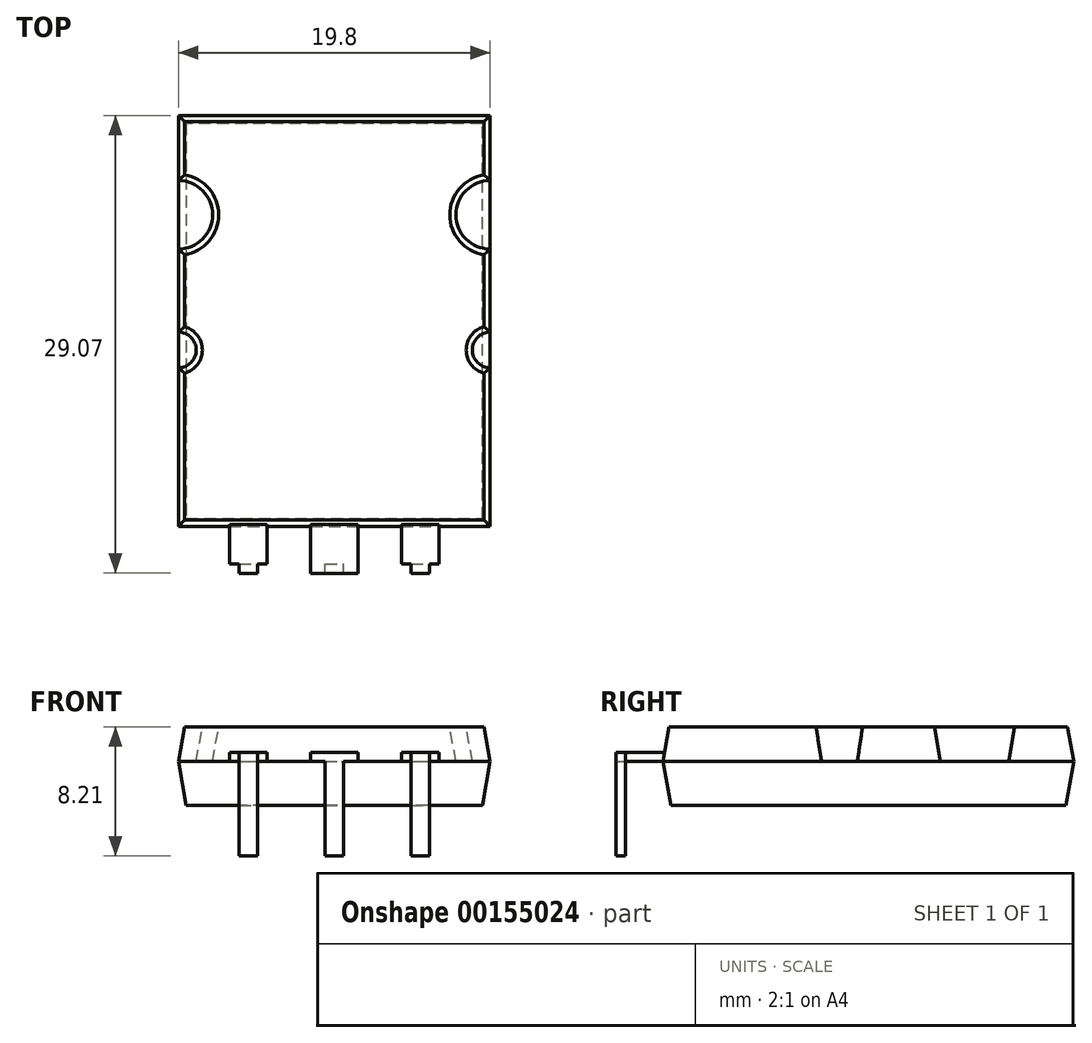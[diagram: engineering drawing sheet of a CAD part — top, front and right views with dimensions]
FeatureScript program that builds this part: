
annotation { "Feature Type Name" : "Feature", "Feature Type Description" : "" }
export const myFeature = defineFeature(function(context is Context, id is Id, definition is map)
    precondition{}
    {
        {
            assignVariable(context, id + "F0", {"name" : "A", "anyValue" : 5});
        }
        {
            assignVariable(context, id + "F1", {"name" : "A1", "anyValue" : 2.8});
        }
        {
            assignVariable(context, id + "F2", {"name" : "c", "anyValue" : .585});
        }
        {
            var Q0;
            Q0=qCreatedBy(makeId("Top.planeOp"),FACE);
            var sketch = newSketch(context, id + "F3", { "sketchPlane" : qUnion([Q0])});
            skLineSegment(sketch, "E0.right", {"start": v(9.9, 26.09) * mm, "end": v(9.9, 21.96) * mm});
            skArc(sketch, "E1", {"start": v(9.9, 21.96) * mm, "mid": v(7.73, 19.79) * mm, "end": v(9.9, 17.61) * mm});
            skArc(sketch, "E2", {"start": v(9.9, 12.33) * mm, "mid": v(8.77, 11.2) * mm, "end": v(9.9, 10.07) * mm});
            skLineSegment(sketch, "E3.trimOffspring", {"start": v(9.9, 17.61) * mm, "end": v(9.9, 12.33) * mm});
            skLineSegment(sketch, "E4.trimOffspring", {"start": v(9.9, 10.07) * mm, "end": v(9.9, 0) * mm});
            skArc(sketch, "E5.MirrorCS", {"start": v(-9.9, 12.33) * mm, "mid": v(-8.77, 11.2) * mm, "end": v(-9.9, 10.07) * mm});
            skLineSegment(sketch, "E6.MirrorCS", {"start": v(-9.9, 17.61) * mm, "end": v(-9.9, 12.33) * mm});
            skArc(sketch, "E7.MirrorCS", {"start": v(-9.9, 21.96) * mm, "mid": v(-7.73, 19.79) * mm, "end": v(-9.9, 17.61) * mm});
            skLineSegment(sketch, "E8.MirrorCS", {"start": v(-9.9, 26.09) * mm, "end": v(-9.9, 21.96) * mm});
            skLineSegment(sketch, "E9.MirrorCS", {"start": v(-9.9, 10.07) * mm, "end": v(-9.9, 0) * mm});
            skLineSegment(sketch, "E10", {"start": v(-9.9, 26.08) * mm, "end": v(9.9, 26.09) * mm});
            skLineSegment(sketch, "E11", {"start": v(9.9, 0) * mm, "end": v(-9.9, 0) * mm});
            skSolve(sketch);
        }
        {
            var Q0;
            Q0 = qSketchRegion(id + "F3", true);
            extrude(context, id + "F4", {"entities" : qUnion([Q0]), "depth" : (getVariable(context, 'A') - getVariable(context, 'A1')) * mm, "hasDraft" : true, "draftAngle" : 10 * degree, "draftPullDirection" : true});
        }
        {
            var Q0;
            Q0=makeQuery(id+"F3.imprint","IMPRINT",FACE,{"disambiguationData":[TD([[makeQuery(id+"F3.imprint","IMPRINT",EDGE,{"derivedFrom":sQuery(id+"F3.wireOp",EDGE,"E0.right")}),-1.0]])]});
            var sketch = newSketch(context, id + "F5", { "sketchPlane" : qUnion([Q0])});
            skLineSegment(sketch, "E12.bottom", {"start": v(-1.5, 0) * mm, "end": v(1.5, 0) * mm});
            skLineSegment(sketch, "E12.top", {"start": v(-1.5, -2.98) * mm, "end": v(1.5, -2.98) * mm});
            skLineSegment(sketch, "E12.left", {"start": v(-1.5, 0) * mm, "end": v(-1.5, -2.98) * mm});
            skLineSegment(sketch, "E12.right", {"start": v(1.5, 0) * mm, "end": v(1.5, -2.98) * mm});
            skLineSegment(sketch, "E13.bottom", {"start": v(-6.66, 0) * mm, "end": v(-4.26, 0) * mm});
            skLineSegment(sketch, "E13.top", {"start": v(-6.04, -2.98) * mm, "end": v(-4.87, -2.98) * mm});
            skLineSegment(sketch, "E13.left", {"start": v(-6.66, 0) * mm, "end": v(-6.66, -2.4) * mm});
            skLineSegment(sketch, "E13.right", {"start": v(-4.26, 0) * mm, "end": v(-4.26, -2.4) * mm});
            skPoint(sketch, "E14", {"position": v(-5.46, 0) * mm});
            skPoint(sketch, "E15", {"position": v(0, 0) * mm});
            skLineSegment(sketch, "E16.bottom", {"start": v(-4.26, 0) * mm, "end": v(-6.66, 0) * mm});
            skLineSegment(sketch, "E16.top", {"start": v(-4.26, 0.94) * mm, "end": v(-6.66, 0.94) * mm});
            skLineSegment(sketch, "E16.left", {"start": v(-4.26, 0) * mm, "end": v(-4.26, 0.94) * mm});
            skLineSegment(sketch, "E16.right", {"start": v(-6.66, 0) * mm, "end": v(-6.66, 0.94) * mm});
            skLineSegment(sketch, "E17.top", {"start": v(-1.5, 0.94) * mm, "end": v(1.5, 0.94) * mm});
            skLineSegment(sketch, "E17.left", {"start": v(-1.5, 0) * mm, "end": v(-1.5, 0.94) * mm});
            skLineSegment(sketch, "E17.right", {"start": v(1.5, 0) * mm, "end": v(1.5, 0.94) * mm});
            skLineSegment(sketch, "E18", {"start": v(-6.66, -2.4) * mm, "end": v(-6.04, -2.4) * mm});
            skLineSegment(sketch, "E19", {"start": v(-6.04, -2.4) * mm, "end": v(-6.04, -2.98) * mm});
            skLineSegment(sketch, "E20", {"start": v(-4.26, -2.4) * mm, "end": v(-4.87, -2.4) * mm});
            skLineSegment(sketch, "E21", {"start": v(-4.87, -2.4) * mm, "end": v(-4.87, -2.98) * mm});
            skLineSegment(sketch, "E22.MirrorCS", {"start": v(6.04, -2.98) * mm, "end": v(4.87, -2.98) * mm});
            skLineSegment(sketch, "E23.MirrorCS", {"start": v(6.04, -2.4) * mm, "end": v(6.04, -2.98) * mm});
            skLineSegment(sketch, "E24.MirrorCS", {"start": v(4.87, -2.4) * mm, "end": v(4.87, -2.98) * mm});
            skLineSegment(sketch, "E25.MirrorCS", {"start": v(6.66, 0) * mm, "end": v(4.26, 0) * mm});
            skLineSegment(sketch, "E26.MirrorCS", {"start": v(4.26, 0) * mm, "end": v(4.26, 0.94) * mm});
            skLineSegment(sketch, "E27.MirrorCS", {"start": v(6.66, 0) * mm, "end": v(6.66, 0.94) * mm});
            skLineSegment(sketch, "E28.MirrorCS", {"start": v(6.66, -2.4) * mm, "end": v(6.04, -2.4) * mm});
            skLineSegment(sketch, "E29.MirrorCS", {"start": v(4.26, -2.4) * mm, "end": v(4.87, -2.4) * mm});
            skLineSegment(sketch, "E30.MirrorCS", {"start": v(6.66, 0) * mm, "end": v(6.66, -2.4) * mm});
            skLineSegment(sketch, "E31.MirrorCS", {"start": v(4.26, 0) * mm, "end": v(6.66, 0) * mm});
            skPoint(sketch, "E32.MirrorP", {"position": v(5.46, 0) * mm});
            skLineSegment(sketch, "E33.MirrorCS", {"start": v(4.26, 0.94) * mm, "end": v(6.66, 0.94) * mm});
            skLineSegment(sketch, "E34.MirrorCS", {"start": v(4.26, 0) * mm, "end": v(4.26, -2.4) * mm});
            skSolve(sketch);
        }
        {
            var Q0;
            Q0 = qSketchRegion(id + "F5", true);
            extrude(context, id + "F6", {"entities" : qUnion([Q0]), "operationType" : NewBodyOperationType.ADD, "depth" : (getVariable(context, 'c')) * mm});
        }
        {
            var Q0;
            Q0=makeQuery(id+"F3.imprint","IMPRINT",FACE,{"disambiguationData":[TD([[makeQuery(id+"F3.imprint","IMPRINT",EDGE,{"derivedFrom":sQuery(id+"F3.wireOp",EDGE,"E0.right")}),-1.0]])]});
            var sketch = newSketch(context, id + "F7", { "sketchPlane" : qUnion([Q0])});
            skLineSegment(sketch, "E35.0", {"start": v(-9.9, 26.08) * mm, "end": v(9.9, 26.09) * mm});
            skLineSegment(sketch, "E35.1", {"start": v(9.9, 0) * mm, "end": v(-9.9, 0) * mm});
            skLineSegment(sketch, "E36", {"start": v(-9.9, 26.08) * mm, "end": v(-9.9, 0) * mm});
            skLineSegment(sketch, "E37", {"start": v(9.9, 0) * mm, "end": v(9.9, 26.09) * mm});
            skSolve(sketch);
        }
        {
            var Q0;
            Q0 = qSketchRegion(id + "F7", true);
            extrude(context, id + "F8", {"entities" : qUnion([Q0]), "operationType" : NewBodyOperationType.ADD, "oppositeDirection" : true, "depth" : (getVariable(context, 'A1')) * mm, "hasDraft" : true, "draftAngle" : 10 * degree, "draftPullDirection" : true});
        }
        {
            var Q0;
            {var subQ0=sQuery(id+"F5.wireOp",EDGE,"E16.left");var subQ1=sQuery(id+"F5.wireOp",EDGE,"E13.right");var subQ2=sQuery(id+"F5.wireOp",EDGE,"E16.right");var subQ3=sQuery(id+"F5.wireOp",EDGE,"E13.left");var subQ4=sQuery(id+"F5.wireOp",EDGE,"E13.top");var subQ5=sQuery(id+"F3.wireOp",EDGE,"E11");Q0=makeQuery(id+"F8.boolean.opBoolean","SPLIT",FACE,{"disambiguationData":[TD([makeQuery(id+"F6.opExtrude","SWEPT_FACE",FACE,{"disambiguationData":[OSD([subQ4])]})])],"derivedFrom":makeQuery(id+"F6.boolean.opBoolean","MERGE",FACE,{"derivedFrom":[makeQuery(id+"F4.opExtrude","CAP_FACE",FACE,{"disambiguationData":[OSD([sQuery(id+"F3.wireOp",EDGE,"E0.right"),sQuery(id+"F3.wireOp",EDGE,"E1"),sQuery(id+"F3.wireOp",EDGE,"E2"),sQuery(id+"F3.wireOp",EDGE,"E3.trimOffspring"),sQuery(id+"F3.wireOp",EDGE,"E4.trimOffspring"),sQuery(id+"F3.wireOp",EDGE,"E5.MirrorCS"),sQuery(id+"F3.wireOp",EDGE,"E6.MirrorCS"),sQuery(id+"F3.wireOp",EDGE,"E7.MirrorCS"),sQuery(id+"F3.wireOp",EDGE,"E8.MirrorCS"),sQuery(id+"F3.wireOp",EDGE,"E9.MirrorCS"),sQuery(id+"F3.wireOp",EDGE,"E10"),subQ5])],"isStart":true}),makeQuery(id+"F6.opExtrude","CAP_FACE",FACE,{"disambiguationData":[OSD([sQuery(id+"F5.wireOp",EDGE,"E12.top"),sQuery(id+"F5.wireOp",EDGE,"E12.left"),sQuery(id+"F5.wireOp",EDGE,"E12.right"),sQuery(id+"F5.wireOp",EDGE,"E17.top"),sQuery(id+"F5.wireOp",EDGE,"E17.left"),sQuery(id+"F5.wireOp",EDGE,"E17.right")])],"isStart":true}),makeQuery(id+"F6.opExtrude","CAP_FACE",FACE,{"disambiguationData":[OSD([subQ4,subQ3,subQ1,sQuery(id+"F5.wireOp",EDGE,"E16.top"),subQ0,subQ2])],"isStart":true}),makeQuery(id+"F6.opExtrude","CAP_FACE",FACE,{"disambiguationData":[OSD([sQuery(id+"F5.wireOp",EDGE,"c1c62ce4-7b16-4c82-a987-7c662a7c0c5f1.MirrorCS"),sQuery(id+"F5.wireOp",EDGE,"c1c62ce4-7b16-4c82-a987-7c662a7c0c5f3.MirrorCS"),sQuery(id+"F5.wireOp",EDGE,"c1c62ce4-7b16-4c82-a987-7c662a7c0c5f4.MirrorCS"),sQuery(id+"F5.wireOp",EDGE,"Yhi3ASPV-syl0-fZz5-beuC-6C4OXgQFjivM.top"),sQuery(id+"F5.wireOp",EDGE,"Yhi3ASPV-syl0-fZz5-beuC-6C4OXgQFjivM.left"),sQuery(id+"F5.wireOp",EDGE,"Yhi3ASPV-syl0-fZz5-beuC-6C4OXgQFjivM.right")])],"isStart":true})]})});}
            var sketch = newSketch(context, id + "F9", { "sketchPlane" : qUnion([Q0])});
            skLineSegment(sketch, "E38.0", {"start": v(-1.5, 2.98) * mm, "end": v(1.5, 2.98) * mm, "construction": true});
            skPoint(sketch, "E39", {"position": v(0, 2.98) * mm});
            skLineSegment(sketch, "E40.bottom", {"start": v(-0.58, 2.98) * mm, "end": v(0.59, 2.98) * mm});
            skLineSegment(sketch, "E40.top", {"start": v(-0.58, 2.4) * mm, "end": v(0.59, 2.4) * mm});
            skLineSegment(sketch, "E40.left", {"start": v(-0.58, 2.98) * mm, "end": v(-0.58, 2.4) * mm});
            skLineSegment(sketch, "E40.right", {"start": v(0.59, 2.98) * mm, "end": v(0.59, 2.4) * mm});
            skPoint(sketch, "E41.0", {"position": v(4.87, 2.4) * mm});
            skLineSegment(sketch, "E42", {"start": v(-6.04, 2.4) * mm, "end": v(-4.87, 2.4) * mm});
            skLineSegment(sketch, "E43.0", {"start": v(4.87, 2.4) * mm, "end": v(4.87, 2.98) * mm});
            skLineSegment(sketch, "E44.0", {"start": v(6.04, 2.98) * mm, "end": v(4.87, 2.98) * mm});
            skLineSegment(sketch, "E45.0", {"start": v(6.04, 2.4) * mm, "end": v(6.04, 2.98) * mm});
            skLineSegment(sketch, "E46.0", {"start": v(-4.87, 2.4) * mm, "end": v(-4.87, 2.98) * mm});
            skLineSegment(sketch, "E47.0", {"start": v(-6.04, 2.98) * mm, "end": v(-4.87, 2.98) * mm});
            skLineSegment(sketch, "E48.0", {"start": v(-6.04, 2.4) * mm, "end": v(-6.04, 2.98) * mm});
            skLineSegment(sketch, "E49", {"start": v(4.87, 2.4) * mm, "end": v(6.04, 2.4) * mm});
            skSolve(sketch);
        }
        {
            var Q0;
            Q0 = qSketchRegion(id + "F9", true);
            extrude(context, id + "F10", {"entities" : qUnion([Q0]), "operationType" : NewBodyOperationType.ADD, "depth" : 6 * mm});
        }
    });
